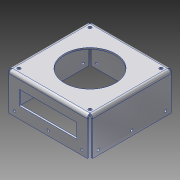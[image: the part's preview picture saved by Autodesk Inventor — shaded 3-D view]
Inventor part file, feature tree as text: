
AUTODESK INVENTOR PART (.ipt)
format: ipt  version: 2015 (Build 190159000, 159)  size: 337,920 bytes
history: native  units: in
note: dims shown in document units (in); Inventor stores cm internally (conversion verified against a paired STEP export)
features: other x6, sketch x5, sheet_metal_op x4, hole x3, projected_geometry x2
ambient origin geometry x8: Origin, YZ Plane, XZ Plane, XY Plane, X Axis, Y Axis, Z Axis, Center Point
bodies: Solid1 (feature_tree)
feature tree (20):
  sketch  "Sketch1"  dims[d4=0.133in d5=0.133in]
  sheet_metal_op  "Face1"
  hole  "Hole1"  [1 undecoded]
  sheet_metal_op  "Flange2"
  other  "A-Side Definition"
  hole  "Hole3"  [1 undecoded]
  hole  "Hole4"  [1 undecoded]
  other  "Plate1"
  sketch  "Sketch3"  dims[d6=0.047in d7=0.047in]
  other  "Plate3"
  sheet_metal_op  "Bend2"
  sheet_metal_op  "Corner2"
  sketch  "Sketch8"  dims[d8=0.133in d9=0.047in]
  sketch  "Sketch9"  dims[d10=2.34in]
  projected_geometry  "Projected Loop9"
  sketch  "Sketch10"  dims[d11=2.34in d12=0.047in d13=0.133in d14=0.047in d15=0.133in d16=6.063in d17=6.063in d18=0.117in d19=0.25in d20=0.25in d21=0.25in d22=0.578in d23=0.25in d24=0.625in d25=0.625in d26=5.68in d27=0.25in d28=5.813in d29=5.813in d30=5.766in d31=0.625in d32=5.813in d33=5.813in d34=0.6915in d35=3.0315in d36=3.0315in d37=3.0315in d38=0.203in d39=5.438in d40=0.25in d41=0.25in d42=0.117in d43=5.813in d44=0.25in d45=0.25in d46=5.391in d47=5.813in d48=5.438in d49=5.438in d50=5.68in d51=5.813in d52=5.813in d53=5.813in d54=4.0in d55=0.125in d56=0.125in d57=0.0in d58=0.25in d59=0.75in d60=0.375in d61=0.25in d62=0.5635in d63=0.125in d64=0.8108in d75=0.125in d76=0.0625in d77=0.25in d78=0.125in d79=2.936in d80=90.0deg d81=0.125in d82=0.5in d83=0.125in d84=0.125in d85=0.3937in d100=0.25in d146=4.5in d147=1.125in d148=0.125in d149=0.0in d150=2.686in d151=0.25in d152=2.936in d153=0.625in d154=0.505in d155=6.1362in d156=0.4375in d157=0.4375in d158=6.1362in d159=0.177in d160=0.177in d161=0.177in d162=0.177in d163=0.75in d164=0.332in d165=0.25in d166=0.5635in d167=0.125in d168=0.8108in d169=0.625in d170=0.505in d171=0.875in d172=0.875in d173=6.1362in d174=6.1362in d175=0.177in d176=0.177in d177=0.177in d178=0.177in d179=0.75in d180=0.332in d181=0.25in d182=0.5635in d183=0.125in d184=0.8108in]
  projected_geometry  "Projected Loop10"
  other  "Cut1"
  other  "Cut2"
  other  "Definition1"
note: 3 required parameter values undecoded (feature->parameter linkage not recoverable at this tier; creation-order binding heuristic only, values carry confidence <= 0.55)
